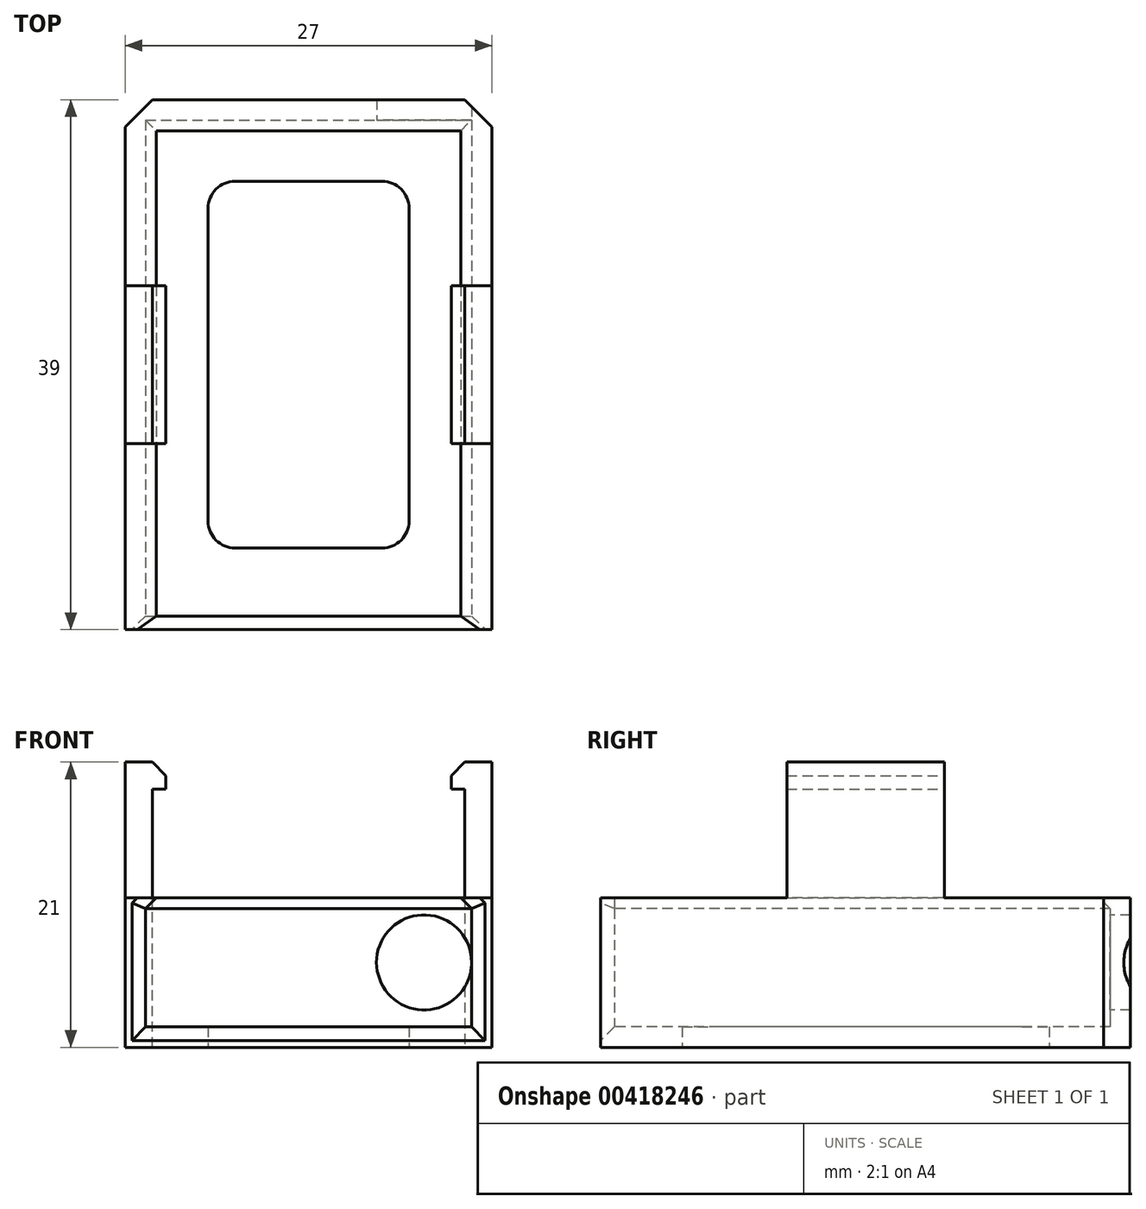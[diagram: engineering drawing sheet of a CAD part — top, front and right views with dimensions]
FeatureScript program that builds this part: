
annotation { "Feature Type Name" : "Feature", "Feature Type Description" : "" }
export const myFeature = defineFeature(function(context is Context, id is Id, definition is map)
    precondition{}
    {
        {
            var Q0;
            Q0=qCreatedBy(makeId("Top.planeOp"),FACE);
            var sketch = newSketch(context, id + "F0", { "sketchPlane" : qUnion([Q0])});
            skPoint(sketch, "E0", {"position": v(0, 0) * mm});
            skLineSegment(sketch, "E1", {"start": v(-12, 19.5) * mm, "end": v(-12, -19.5) * mm});
            skLineSegment(sketch, "E2.MirrorCS", {"start": v(12, 19.5) * mm, "end": v(12, -19.5) * mm});
            skLineSegment(sketch, "E3", {"start": v(-13.5, 19.5) * mm, "end": v(-13.5, -19.5) * mm});
            skLineSegment(sketch, "E4.MirrorCS", {"start": v(13.5, 19.5) * mm, "end": v(13.5, -19.5) * mm});
            skLineSegment(sketch, "E5", {"start": v(-13.5, 19.5) * mm, "end": v(13.5, 19.5) * mm});
            skLineSegment(sketch, "E6.MirrorCS", {"start": v(-13.5, -19.5) * mm, "end": v(13.5, -19.5) * mm});
            skLineSegment(sketch, "E7", {"start": v(-12, 18) * mm, "end": v(12, 18) * mm});
            skLineSegment(sketch, "E8.bottom", {"start": v(7.4, 13.5) * mm, "end": v(-7.4, 13.5) * mm});
            skLineSegment(sketch, "E8.top", {"start": v(7.4, -13.5) * mm, "end": v(-7.4, -13.5) * mm});
            skLineSegment(sketch, "E8.left", {"start": v(7.4, 13.5) * mm, "end": v(7.4, -13.5) * mm});
            skLineSegment(sketch, "E8.right", {"start": v(-7.4, 13.5) * mm, "end": v(-7.4, -13.5) * mm});
            skLineSegment(sketch, "E9", {"start": v(-11.5, 0) * mm, "end": v(-11.5, 5.8) * mm});
            skLineSegment(sketch, "E10.MirrorCS", {"start": v(-11.5, 0) * mm, "end": v(-11.5, -5.8) * mm});
            skLineSegment(sketch, "E11.MirrorCS", {"start": v(11.5, 0) * mm, "end": v(11.5, 5.8) * mm});
            skLineSegment(sketch, "E12.MirrorCS", {"start": v(11.5, 0) * mm, "end": v(11.5, -5.8) * mm});
            skLineSegment(sketch, "E13", {"start": v(-11.5, 5.8) * mm, "end": v(-13.5, 5.8) * mm});
            skLineSegment(sketch, "E14", {"start": v(-11.5, -5.8) * mm, "end": v(-13.5, -5.8) * mm});
            skLineSegment(sketch, "E15", {"start": v(11.5, 5.8) * mm, "end": v(13.5, 5.8) * mm});
            skLineSegment(sketch, "E16", {"start": v(11.5, -5.8) * mm, "end": v(13.5, -5.8) * mm});
            skSolve(sketch);
        }
        {
            var Q0;
            {var subQ0=sQuery(id+"F0.wireOp",EDGE,"E7");Q0=makeQuery(id+"F0.imprint","IMPRINT",FACE,{"disambiguationData":[TD([[makeQuery(id+"F0.imprint","IMPRINT",EDGE,{"derivedFrom":subQ0}),-1.0]])]});}
            extrude(context, id + "F1", {"entities" : qUnion([Q0]), "depth" : 1.5 * mm});
        }
        {
            var Q0;
            {var subQ1=sQuery(id+"F0.wireOp",EDGE,"E9");Q0=makeQuery(id+"F0.imprint","IMPRINT",FACE,{"disambiguationData":[TD([[makeQuery(id+"F0.imprint","IMPRINT",EDGE,{"derivedFrom":subQ1}),1.0]])]});}
            var Q1;
            {var subQ0=sQuery(id+"F0.wireOp",EDGE,"E13");var subQ1=sQuery(id+"F0.wireOp",EDGE,"E1");var subQ2=makeQuery(id+"F0.imprint","INTERSECT",VERTEX,{"derivedFrom":[subQ1,subQ0]});Q1=makeQuery(id+"F0.imprint","IMPRINT",FACE,{"disambiguationData":[TD([[makeQuery(id+"F0.imprint","IMPRINT",EDGE,{"disambiguationData":[TD([[subQ2,-1.0]])],"derivedFrom":subQ1}),-1.0]])]});}
            var Q2;
            {var subQ1=sQuery(id+"F0.wireOp",EDGE,"E11.MirrorCS");Q2=makeQuery(id+"F0.imprint","IMPRINT",FACE,{"disambiguationData":[TD([[makeQuery(id+"F0.imprint","IMPRINT",EDGE,{"derivedFrom":subQ1}),-1.0]])]});}
            var Q3;
            {var subQ0=sQuery(id+"F0.wireOp",EDGE,"E15");var subQ1=sQuery(id+"F0.wireOp",EDGE,"E2.MirrorCS");var subQ2=makeQuery(id+"F0.imprint","INTERSECT",VERTEX,{"derivedFrom":[subQ1,subQ0]});Q3=makeQuery(id+"F0.imprint","IMPRINT",FACE,{"disambiguationData":[TD([[makeQuery(id+"F0.imprint","IMPRINT",EDGE,{"disambiguationData":[TD([[subQ2,-1.0]])],"derivedFrom":subQ1}),1.0]])]});}
            extrude(context, id + "F2", {"entities" : qUnion([Q0, Q1, Q2, Q3]), "operationType" : NewBodyOperationType.ADD, "depth" : 21 * mm});
        }
        {
            var Q0;
            {var subQ3=sQuery(id+"F0.wireOp",EDGE,"E7");Q0=makeQuery(id+"F0.imprint","IMPRINT",FACE,{"disambiguationData":[TD([[makeQuery(id+"F0.imprint","IMPRINT",EDGE,{"derivedFrom":subQ3}),1.0]])]});}
            var Q1;
            {var subQ0=sQuery(id+"F0.wireOp",EDGE,"E5");var subQ1=sQuery(id+"F0.wireOp",EDGE,"E1");var subQ2=makeQuery(id+"F0.imprint","INTERSECT",VERTEX,{"derivedFrom":[subQ1,subQ0]});Q1=makeQuery(id+"F0.imprint","IMPRINT",FACE,{"disambiguationData":[TD([[makeQuery(id+"F0.imprint","IMPRINT",EDGE,{"disambiguationData":[TD([[subQ2,-1.0]])],"derivedFrom":subQ1}),-1.0]])]});}
            var Q2;
            {var subQ0=sQuery(id+"F0.wireOp",EDGE,"E6.MirrorCS");var subQ1=sQuery(id+"F0.wireOp",EDGE,"E1");var subQ2=makeQuery(id+"F0.imprint","INTERSECT",VERTEX,{"derivedFrom":[subQ1,subQ0]});Q2=makeQuery(id+"F0.imprint","IMPRINT",FACE,{"disambiguationData":[TD([[makeQuery(id+"F0.imprint","IMPRINT",EDGE,{"disambiguationData":[TD([[subQ2,1.0]])],"derivedFrom":subQ1}),-1.0]])]});}
            var Q3;
            {var subQ0=sQuery(id+"F0.wireOp",EDGE,"E6.MirrorCS");var subQ1=sQuery(id+"F0.wireOp",EDGE,"E2.MirrorCS");var subQ2=makeQuery(id+"F0.imprint","INTERSECT",VERTEX,{"derivedFrom":[subQ1,subQ0]});Q3=makeQuery(id+"F0.imprint","IMPRINT",FACE,{"disambiguationData":[TD([[makeQuery(id+"F0.imprint","IMPRINT",EDGE,{"disambiguationData":[TD([[subQ2,1.0]])],"derivedFrom":subQ1}),1.0]])]});}
            var Q4;
            {var subQ0=sQuery(id+"F0.wireOp",EDGE,"E5");var subQ1=sQuery(id+"F0.wireOp",EDGE,"E2.MirrorCS");var subQ2=makeQuery(id+"F0.imprint","INTERSECT",VERTEX,{"derivedFrom":[subQ1,subQ0]});Q4=makeQuery(id+"F0.imprint","IMPRINT",FACE,{"disambiguationData":[TD([[makeQuery(id+"F0.imprint","IMPRINT",EDGE,{"disambiguationData":[TD([[subQ2,-1.0]])],"derivedFrom":subQ1}),1.0]])]});}
            extrude(context, id + "F3", {"entities" : qUnion([Q0, Q1, Q2, Q3, Q4]), "operationType" : NewBodyOperationType.ADD, "depth" : 11 * mm});
        }
        {
            var Q0;
            {var subQ1=sQuery(id+"F0.wireOp",EDGE,"E9");Q0=makeQuery(id+"F0.imprint","IMPRINT",FACE,{"disambiguationData":[TD([[makeQuery(id+"F0.imprint","IMPRINT",EDGE,{"derivedFrom":subQ1}),1.0]])]});}
            var Q1;
            {var subQ1=sQuery(id+"F0.wireOp",EDGE,"E11.MirrorCS");Q1=makeQuery(id+"F0.imprint","IMPRINT",FACE,{"disambiguationData":[TD([[makeQuery(id+"F0.imprint","IMPRINT",EDGE,{"derivedFrom":subQ1}),-1.0]])]});}
            extrude(context, id + "F4", {"entities" : qUnion([Q0, Q1]), "operationType" : NewBodyOperationType.REMOVE, "depth" : 11 * mm, "hasSecondDirection" : true, "secondDirectionOppositeDirection" : false, "secondDirectionDepth" : 1.5 * mm});
        }
        {
            var Q0;
            {var subQ0=sQuery(id+"F0.wireOp",EDGE,"E1");Q0=makeQuery(id+"F4.boolean.opBoolean","MERGE",FACE,{"derivedFrom":[makeQuery(id+"F3.opExtrude","SWEPT_FACE",FACE,{"disambiguationData":[OSD([subQ0]),TDD([makeQuery(id+"F0.imprint","IMPRINT",EDGE,{"disambiguationData":[TD([[makeQuery(id+"F0.imprint","INTERSECT",VERTEX,{"derivedFrom":[subQ0,sQuery(id+"F0.wireOp",EDGE,"E7")]}),-1.0]])],"derivedFrom":subQ0})])]}),makeQuery(id+"F3.opExtrude","SWEPT_FACE",FACE,{"disambiguationData":[OSD([subQ0]),TDD([makeQuery(id+"F0.imprint","IMPRINT",EDGE,{"disambiguationData":[TD([[makeQuery(id+"F0.imprint","INTERSECT",VERTEX,{"derivedFrom":[subQ0,sQuery(id+"F0.wireOp",EDGE,"E6.MirrorCS")]}),1.0]])],"derivedFrom":subQ0})])]}),makeQuery(id+"F4.opExtrude","SWEPT_FACE",FACE,{"disambiguationData":[OSD([subQ0])]})]});}
            var sketch = newSketch(context, id + "F5", { "sketchPlane" : qUnion([Q0])});
            skLineSegment(sketch, "E17", {"start": v(18, 10.2) * mm, "end": v(-19.5, 10.2) * mm});
            skSolve(sketch);
        }
        {
            var Q0;
            Q0=makeQuery(id+"F3.opExtrude","SWEPT_FACE",FACE,{"disambiguationData":[OSD([sQuery(id+"F0.wireOp",EDGE,"E7")])]});
            var sketch = newSketch(context, id + "F6", { "sketchPlane" : qUnion([Q0])});
            skLineSegment(sketch, "E18", {"start": v(-12, 10.2) * mm, "end": v(12, 10.2) * mm});
            skSolve(sketch);
        }
        {
            var Q0;
            {var subQ0=sQuery(id+"F0.wireOp",EDGE,"E2.MirrorCS");Q0=makeQuery(id+"F4.boolean.opBoolean","MERGE",FACE,{"derivedFrom":[makeQuery(id+"F3.opExtrude","SWEPT_FACE",FACE,{"disambiguationData":[OSD([subQ0]),TDD([makeQuery(id+"F0.imprint","IMPRINT",EDGE,{"disambiguationData":[TD([[makeQuery(id+"F0.imprint","INTERSECT",VERTEX,{"derivedFrom":[subQ0,sQuery(id+"F0.wireOp",EDGE,"E7")]}),-1.0]])],"derivedFrom":subQ0})])]}),makeQuery(id+"F3.opExtrude","SWEPT_FACE",FACE,{"disambiguationData":[OSD([subQ0]),TDD([makeQuery(id+"F0.imprint","IMPRINT",EDGE,{"disambiguationData":[TD([[makeQuery(id+"F0.imprint","INTERSECT",VERTEX,{"derivedFrom":[subQ0,sQuery(id+"F0.wireOp",EDGE,"E6.MirrorCS")]}),1.0]])],"derivedFrom":subQ0})])]}),makeQuery(id+"F4.opExtrude","SWEPT_FACE",FACE,{"disambiguationData":[OSD([subQ0])]})]});}
            var sketch = newSketch(context, id + "F7", { "sketchPlane" : qUnion([Q0])});
            skLineSegment(sketch, "E19", {"start": v(-18, 10.2) * mm, "end": v(19.5, 10.2) * mm});
            skSolve(sketch);
        }
        {
            var Q0;
            {var subQ5=sQuery(id+"F7.wireOp",EDGE,"E19");Q0=makeQuery(id+"F7.imprint","IMPRINT",FACE,{"disambiguationData":[TD([[makeQuery(id+"F7.imprint","IMPRINT",EDGE,{"derivedFrom":subQ5}),1.0]])]});}
            var Q1;
            Q1=makeQuery(id+"F2.opExtrude","SWEPT_FACE",FACE,{"disambiguationData":[OSD([sQuery(id+"F0.wireOp",EDGE,"E11.MirrorCS"),sQuery(id+"F0.wireOp",EDGE,"E12.MirrorCS")])]});
            extrude(context, id + "F8", {"entities" : qUnion([Q0]), "operationType" : NewBodyOperationType.ADD, "endBoundEntityFace" : qUnion([Q1]), "depth" : 0.8 * mm});
        }
        {
            var Q0;
            {var subQ5=sQuery(id+"F5.wireOp",EDGE,"E17");Q0=makeQuery(id+"F5.imprint","IMPRINT",FACE,{"disambiguationData":[TD([[makeQuery(id+"F5.imprint","IMPRINT",EDGE,{"derivedFrom":subQ5}),-1.0]])]});}
            extrude(context, id + "F9", {"entities" : qUnion([Q0]), "operationType" : NewBodyOperationType.ADD, "depth" : 0.8 * mm});
        }
        {
            var Q0;
            {var subQ0=sQuery(id+"F6.wireOp",EDGE,"E18");Q0=makeQuery(id+"F6.imprint","IMPRINT",FACE,{"disambiguationData":[TD([[makeQuery(id+"F6.imprint","IMPRINT",EDGE,{"derivedFrom":subQ0}),1.0]])]});}
            extrude(context, id + "F10", {"entities" : qUnion([Q0]), "operationType" : NewBodyOperationType.ADD, "depth" : 0.8 * mm});
        }
        {
            var Q0;
            Q0=makeQuery(id+"F9.opExtrude","CAP_EDGE",EDGE,{"disambiguationData":[OSD([sQuery(id+"F5.wireOp",EDGE,"E17")])],"isStart":false});
            var Q1;
            Q1=makeQuery(id+"F10.opExtrude","CAP_EDGE",EDGE,{"disambiguationData":[OSD([sQuery(id+"F6.wireOp",EDGE,"E18")])],"isStart":false});
            var Q2;
            Q2=makeQuery(id+"F8.opExtrude","CAP_EDGE",EDGE,{"disambiguationData":[OSD([sQuery(id+"F7.wireOp",EDGE,"E19")])],"isStart":false});
            var Q3;
            {var subQ0=sQuery(id+"F0.wireOp",EDGE,"E2.MirrorCS");Q3=makeQuery(id+"F4.boolean.opBoolean","MERGE",EDGE,{"derivedFrom":[makeQuery(id+"F1.opExtrude","CAP_EDGE",EDGE,{"disambiguationData":[OSD([subQ0]),TDD([makeQuery(id+"F0.imprint","IMPRINT",EDGE,{"disambiguationData":[TD([[makeQuery(id+"F0.imprint","INTERSECT",VERTEX,{"derivedFrom":[subQ0,sQuery(id+"F0.wireOp",EDGE,"E7")]}),-1.0]])],"derivedFrom":subQ0})])],"isStart":false}),makeQuery(id+"F1.opExtrude","CAP_EDGE",EDGE,{"disambiguationData":[OSD([subQ0]),TDD([makeQuery(id+"F0.imprint","IMPRINT",EDGE,{"disambiguationData":[TD([[makeQuery(id+"F0.imprint","INTERSECT",VERTEX,{"derivedFrom":[subQ0,sQuery(id+"F0.wireOp",EDGE,"E6.MirrorCS")]}),1.0]])],"derivedFrom":subQ0})])],"isStart":false}),makeQuery(id+"F4.opExtrude","CAP_EDGE",EDGE,{"disambiguationData":[OSD([subQ0])],"isStart":true})]});}
            var Q4;
            {var subQ0=sQuery(id+"F0.wireOp",EDGE,"E1");Q4=makeQuery(id+"F4.boolean.opBoolean","MERGE",EDGE,{"derivedFrom":[makeQuery(id+"F1.opExtrude","CAP_EDGE",EDGE,{"disambiguationData":[OSD([subQ0]),TDD([makeQuery(id+"F0.imprint","IMPRINT",EDGE,{"disambiguationData":[TD([[makeQuery(id+"F0.imprint","INTERSECT",VERTEX,{"derivedFrom":[subQ0,sQuery(id+"F0.wireOp",EDGE,"E7")]}),-1.0]])],"derivedFrom":subQ0})])],"isStart":false}),makeQuery(id+"F1.opExtrude","CAP_EDGE",EDGE,{"disambiguationData":[OSD([subQ0]),TDD([makeQuery(id+"F0.imprint","IMPRINT",EDGE,{"disambiguationData":[TD([[makeQuery(id+"F0.imprint","INTERSECT",VERTEX,{"derivedFrom":[subQ0,sQuery(id+"F0.wireOp",EDGE,"E6.MirrorCS")]}),1.0]])],"derivedFrom":subQ0})])],"isStart":false}),makeQuery(id+"F4.opExtrude","CAP_EDGE",EDGE,{"disambiguationData":[OSD([subQ0])],"isStart":true})]});}
            var Q5;
            Q5=makeQuery(id+"F1.opExtrude","CAP_EDGE",EDGE,{"disambiguationData":[OSD([sQuery(id+"F0.wireOp",EDGE,"E7")])],"isStart":false});
            chamfer(context, id + "F11", {"entities" : qUnion([Q0, Q1, Q2, Q3, Q4, Q5]), "width" : 0.8 * mm, "tangentPropagation" : true});
        }
        {
            var Q0;
            Q0=makeQuery(id+"F3.opExtrude","SWEPT_EDGE",EDGE,{"disambiguationData":[OSD([sQuery(id+"F0.wireOp",EDGE,"E4.MirrorCS"),sQuery(id+"F0.wireOp",EDGE,"E5")])]});
            var Q1;
            Q1=makeQuery(id+"F3.opExtrude","SWEPT_EDGE",EDGE,{"disambiguationData":[OSD([sQuery(id+"F0.wireOp",EDGE,"E3"),sQuery(id+"F0.wireOp",EDGE,"E5")])]});
            chamfer(context, id + "F12", {"entities" : qUnion([Q0, Q1]), "width" : 2 * mm, "tangentPropagation" : true});
        }
        {
            var Q0;
            Q0=makeQuery(id+"F2.opExtrude","SWEPT_FACE",FACE,{"disambiguationData":[OSD([sQuery(id+"F0.wireOp",EDGE,"E9"),sQuery(id+"F0.wireOp",EDGE,"E10.MirrorCS")])]});
            var sketch = newSketch(context, id + "F13", { "sketchPlane" : qUnion([Q0])});
            skLineSegment(sketch, "E20", {"start": v(-5.8, 19) * mm, "end": v(5.8, 19) * mm});
            skSolve(sketch);
        }
        {
            var Q0;
            Q0=makeQuery(id+"F2.opExtrude","SWEPT_FACE",FACE,{"disambiguationData":[OSD([sQuery(id+"F0.wireOp",EDGE,"E11.MirrorCS"),sQuery(id+"F0.wireOp",EDGE,"E12.MirrorCS")])]});
            var sketch = newSketch(context, id + "F14", { "sketchPlane" : qUnion([Q0])});
            skLineSegment(sketch, "E21", {"start": v(5.8, 19) * mm, "end": v(-5.8, 19) * mm});
            skSolve(sketch);
        }
        {
            var Q0;
            {var subQ0=sQuery(id+"F14.wireOp",EDGE,"E21");Q0=makeQuery(id+"F14.imprint","IMPRINT",FACE,{"disambiguationData":[TD([[makeQuery(id+"F14.imprint","IMPRINT",EDGE,{"derivedFrom":subQ0}),-1.0]])]});}
            extrude(context, id + "F15", {"entities" : qUnion([Q0]), "operationType" : NewBodyOperationType.ADD, "depth" : 1 * mm});
        }
        {
            var Q0;
            {var subQ0=sQuery(id+"F13.wireOp",EDGE,"E20");Q0=makeQuery(id+"F13.imprint","IMPRINT",FACE,{"disambiguationData":[TD([[makeQuery(id+"F13.imprint","IMPRINT",EDGE,{"derivedFrom":subQ0}),1.0]])]});}
            extrude(context, id + "F16", {"entities" : qUnion([Q0]), "operationType" : NewBodyOperationType.ADD, "depth" : 1 * mm});
        }
        {
            var Q0;
            Q0=makeQuery(id+"F16.opExtrude","CAP_EDGE",EDGE,{"disambiguationData":[OSD([sQuery(id+"F0.wireOp",EDGE,"E9"),sQuery(id+"F0.wireOp",EDGE,"E10.MirrorCS")])],"isStart":false});
            var Q1;
            Q1=makeQuery(id+"F15.opExtrude","CAP_EDGE",EDGE,{"disambiguationData":[OSD([sQuery(id+"F0.wireOp",EDGE,"E11.MirrorCS"),sQuery(id+"F0.wireOp",EDGE,"E12.MirrorCS")])],"isStart":false});
            chamfer(context, id + "F17", {"entities" : qUnion([Q0, Q1]), "width" : 1 * mm, "tangentPropagation" : true});
        }
        {
            var Q0;
            Q0=makeQuery(id+"F1.opExtrude","CAP_EDGE",EDGE,{"disambiguationData":[OSD([sQuery(id+"F0.wireOp",EDGE,"E6.MirrorCS")])],"isStart":false});
            var Q1;
            Q1=makeQuery(id+"F3.opExtrude","SWEPT_EDGE",EDGE,{"disambiguationData":[OSD([sQuery(id+"F0.wireOp",EDGE,"E2.MirrorCS"),sQuery(id+"F0.wireOp",EDGE,"E6.MirrorCS")])]});
            var Q2;
            {var subQ0=sQuery(id+"F0.wireOp",EDGE,"E6.MirrorCS");var subQ1=sQuery(id+"F0.wireOp",EDGE,"E1");var subQ2=sQuery(id+"F0.wireOp",EDGE,"E2.MirrorCS");var subQ3=makeQuery(id+"F0.imprint","INTERSECT",VERTEX,{"derivedFrom":[subQ2,subQ0]});Q2=makeQuery(id+"F11.opChamfer","BLEND_EDGE",EDGE,{"blendedFrom":[makeQuery(id+"F4.boolean.opBoolean","MERGE",EDGE,{"derivedFrom":[makeQuery(id+"F1.opExtrude","CAP_EDGE",EDGE,{"disambiguationData":[OSD([subQ2]),TDD([makeQuery(id+"F0.imprint","IMPRINT",EDGE,{"disambiguationData":[TD([[makeQuery(id+"F0.imprint","INTERSECT",VERTEX,{"derivedFrom":[subQ2,sQuery(id+"F0.wireOp",EDGE,"E7")]}),-1.0]])],"derivedFrom":subQ2})])],"isStart":false}),makeQuery(id+"F1.opExtrude","CAP_EDGE",EDGE,{"disambiguationData":[OSD([subQ2]),TDD([makeQuery(id+"F0.imprint","IMPRINT",EDGE,{"disambiguationData":[TD([[subQ3,1.0]])],"derivedFrom":subQ2})])],"isStart":false}),makeQuery(id+"F4.opExtrude","CAP_EDGE",EDGE,{"disambiguationData":[OSD([subQ2])],"isStart":true})]}),makeQuery(id+"F9.boolean.opBoolean","MERGE",FACE,{"derivedFrom":[makeQuery(id+"F8.boolean.opBoolean","MERGE",FACE,{"derivedFrom":[makeQuery(id+"F3.boolean.opBoolean","MERGE",FACE,{"derivedFrom":[makeQuery(id+"F1.opExtrude","SWEPT_FACE",FACE,{"disambiguationData":[OSD([subQ0])]}),makeQuery(id+"F3.opExtrude","SWEPT_FACE",FACE,{"disambiguationData":[OSD([subQ0]),TDD([makeQuery(id+"F0.imprint","IMPRINT",EDGE,{"disambiguationData":[TD([[makeQuery(id+"F0.imprint","INTERSECT",VERTEX,{"derivedFrom":[subQ1,subQ0]}),1.0]])],"derivedFrom":subQ0})])]}),makeQuery(id+"F3.opExtrude","SWEPT_FACE",FACE,{"disambiguationData":[OSD([subQ0]),TDD([makeQuery(id+"F0.imprint","IMPRINT",EDGE,{"disambiguationData":[TD([[subQ3,-1.0]])],"derivedFrom":subQ0})])]})]}),makeQuery(id+"F8.opExtrude","SWEPT_FACE",FACE,{"disambiguationData":[OSD([subQ2,subQ0])]})]}),makeQuery(id+"F9.opExtrude","SWEPT_FACE",FACE,{"disambiguationData":[OSD([subQ1,subQ0])]})]})],"blendedInto":[makeQuery(id+"F9.boolean.opBoolean","MERGE",FACE,{"derivedFrom":[makeQuery(id+"F8.boolean.opBoolean","MERGE",FACE,{"derivedFrom":[makeQuery(id+"F3.boolean.opBoolean","MERGE",FACE,{"derivedFrom":[makeQuery(id+"F1.opExtrude","SWEPT_FACE",FACE,{"disambiguationData":[OSD([subQ0])]}),makeQuery(id+"F3.opExtrude","SWEPT_FACE",FACE,{"disambiguationData":[OSD([subQ0]),TDD([makeQuery(id+"F0.imprint","IMPRINT",EDGE,{"disambiguationData":[TD([[makeQuery(id+"F0.imprint","INTERSECT",VERTEX,{"derivedFrom":[subQ1,subQ0]}),1.0]])],"derivedFrom":subQ0})])]}),makeQuery(id+"F3.opExtrude","SWEPT_FACE",FACE,{"disambiguationData":[OSD([subQ0]),TDD([makeQuery(id+"F0.imprint","IMPRINT",EDGE,{"disambiguationData":[TD([[subQ3,-1.0]])],"derivedFrom":subQ0})])]})]}),makeQuery(id+"F8.opExtrude","SWEPT_FACE",FACE,{"disambiguationData":[OSD([subQ2,subQ0])]})]}),makeQuery(id+"F9.opExtrude","SWEPT_FACE",FACE,{"disambiguationData":[OSD([subQ1,subQ0])]})]})]});}
            var Q3;
            Q3=makeQuery(id+"F3.opExtrude","SWEPT_EDGE",EDGE,{"disambiguationData":[OSD([sQuery(id+"F0.wireOp",EDGE,"E1"),sQuery(id+"F0.wireOp",EDGE,"E6.MirrorCS")])]});
            var Q4;
            {var subQ0=sQuery(id+"F0.wireOp",EDGE,"E6.MirrorCS");var subQ1=sQuery(id+"F0.wireOp",EDGE,"E1");var subQ2=sQuery(id+"F0.wireOp",EDGE,"E2.MirrorCS");var subQ3=makeQuery(id+"F0.imprint","INTERSECT",VERTEX,{"derivedFrom":[subQ1,subQ0]});Q4=makeQuery(id+"F11.opChamfer","BLEND_EDGE",EDGE,{"blendedFrom":[makeQuery(id+"F4.boolean.opBoolean","MERGE",EDGE,{"derivedFrom":[makeQuery(id+"F1.opExtrude","CAP_EDGE",EDGE,{"disambiguationData":[OSD([subQ1]),TDD([makeQuery(id+"F0.imprint","IMPRINT",EDGE,{"disambiguationData":[TD([[makeQuery(id+"F0.imprint","INTERSECT",VERTEX,{"derivedFrom":[subQ1,sQuery(id+"F0.wireOp",EDGE,"E7")]}),-1.0]])],"derivedFrom":subQ1})])],"isStart":false}),makeQuery(id+"F1.opExtrude","CAP_EDGE",EDGE,{"disambiguationData":[OSD([subQ1]),TDD([makeQuery(id+"F0.imprint","IMPRINT",EDGE,{"disambiguationData":[TD([[subQ3,1.0]])],"derivedFrom":subQ1})])],"isStart":false}),makeQuery(id+"F4.opExtrude","CAP_EDGE",EDGE,{"disambiguationData":[OSD([subQ1])],"isStart":true})]}),makeQuery(id+"F9.boolean.opBoolean","MERGE",FACE,{"derivedFrom":[makeQuery(id+"F8.boolean.opBoolean","MERGE",FACE,{"derivedFrom":[makeQuery(id+"F3.boolean.opBoolean","MERGE",FACE,{"derivedFrom":[makeQuery(id+"F1.opExtrude","SWEPT_FACE",FACE,{"disambiguationData":[OSD([subQ0])]}),makeQuery(id+"F3.opExtrude","SWEPT_FACE",FACE,{"disambiguationData":[OSD([subQ0]),TDD([makeQuery(id+"F0.imprint","IMPRINT",EDGE,{"disambiguationData":[TD([[subQ3,1.0]])],"derivedFrom":subQ0})])]}),makeQuery(id+"F3.opExtrude","SWEPT_FACE",FACE,{"disambiguationData":[OSD([subQ0]),TDD([makeQuery(id+"F0.imprint","IMPRINT",EDGE,{"disambiguationData":[TD([[makeQuery(id+"F0.imprint","INTERSECT",VERTEX,{"derivedFrom":[subQ2,subQ0]}),-1.0]])],"derivedFrom":subQ0})])]})]}),makeQuery(id+"F8.opExtrude","SWEPT_FACE",FACE,{"disambiguationData":[OSD([subQ2,subQ0])]})]}),makeQuery(id+"F9.opExtrude","SWEPT_FACE",FACE,{"disambiguationData":[OSD([subQ1,subQ0])]})]})],"blendedInto":[makeQuery(id+"F9.boolean.opBoolean","MERGE",FACE,{"derivedFrom":[makeQuery(id+"F8.boolean.opBoolean","MERGE",FACE,{"derivedFrom":[makeQuery(id+"F3.boolean.opBoolean","MERGE",FACE,{"derivedFrom":[makeQuery(id+"F1.opExtrude","SWEPT_FACE",FACE,{"disambiguationData":[OSD([subQ0])]}),makeQuery(id+"F3.opExtrude","SWEPT_FACE",FACE,{"disambiguationData":[OSD([subQ0]),TDD([makeQuery(id+"F0.imprint","IMPRINT",EDGE,{"disambiguationData":[TD([[subQ3,1.0]])],"derivedFrom":subQ0})])]}),makeQuery(id+"F3.opExtrude","SWEPT_FACE",FACE,{"disambiguationData":[OSD([subQ0]),TDD([makeQuery(id+"F0.imprint","IMPRINT",EDGE,{"disambiguationData":[TD([[makeQuery(id+"F0.imprint","INTERSECT",VERTEX,{"derivedFrom":[subQ2,subQ0]}),-1.0]])],"derivedFrom":subQ0})])]})]}),makeQuery(id+"F8.opExtrude","SWEPT_FACE",FACE,{"disambiguationData":[OSD([subQ2,subQ0])]})]}),makeQuery(id+"F9.opExtrude","SWEPT_FACE",FACE,{"disambiguationData":[OSD([subQ1,subQ0])]})]})]});}
            var Q5;
            {var subQ0=sQuery(id+"F0.wireOp",EDGE,"E6.MirrorCS");var subQ1=sQuery(id+"F0.wireOp",EDGE,"E1");var subQ2=sQuery(id+"F0.wireOp",EDGE,"E2.MirrorCS");Q5=makeQuery(id+"F11.opChamfer","BLEND_EDGE",EDGE,{"blendedFrom":[makeQuery(id+"F9.opExtrude","CAP_EDGE",EDGE,{"disambiguationData":[OSD([sQuery(id+"F5.wireOp",EDGE,"E17")])],"isStart":false}),makeQuery(id+"F9.boolean.opBoolean","MERGE",FACE,{"derivedFrom":[makeQuery(id+"F8.boolean.opBoolean","MERGE",FACE,{"derivedFrom":[makeQuery(id+"F3.boolean.opBoolean","MERGE",FACE,{"derivedFrom":[makeQuery(id+"F1.opExtrude","SWEPT_FACE",FACE,{"disambiguationData":[OSD([subQ0])]}),makeQuery(id+"F3.opExtrude","SWEPT_FACE",FACE,{"disambiguationData":[OSD([subQ0]),TDD([makeQuery(id+"F0.imprint","IMPRINT",EDGE,{"disambiguationData":[TD([[makeQuery(id+"F0.imprint","INTERSECT",VERTEX,{"derivedFrom":[subQ1,subQ0]}),1.0]])],"derivedFrom":subQ0})])]}),makeQuery(id+"F3.opExtrude","SWEPT_FACE",FACE,{"disambiguationData":[OSD([subQ0]),TDD([makeQuery(id+"F0.imprint","IMPRINT",EDGE,{"disambiguationData":[TD([[makeQuery(id+"F0.imprint","INTERSECT",VERTEX,{"derivedFrom":[subQ2,subQ0]}),-1.0]])],"derivedFrom":subQ0})])]})]}),makeQuery(id+"F8.opExtrude","SWEPT_FACE",FACE,{"disambiguationData":[OSD([subQ2,subQ0])]})]}),makeQuery(id+"F9.opExtrude","SWEPT_FACE",FACE,{"disambiguationData":[OSD([subQ1,subQ0])]})]})],"blendedInto":[makeQuery(id+"F9.boolean.opBoolean","MERGE",FACE,{"derivedFrom":[makeQuery(id+"F8.boolean.opBoolean","MERGE",FACE,{"derivedFrom":[makeQuery(id+"F3.boolean.opBoolean","MERGE",FACE,{"derivedFrom":[makeQuery(id+"F1.opExtrude","SWEPT_FACE",FACE,{"disambiguationData":[OSD([subQ0])]}),makeQuery(id+"F3.opExtrude","SWEPT_FACE",FACE,{"disambiguationData":[OSD([subQ0]),TDD([makeQuery(id+"F0.imprint","IMPRINT",EDGE,{"disambiguationData":[TD([[makeQuery(id+"F0.imprint","INTERSECT",VERTEX,{"derivedFrom":[subQ1,subQ0]}),1.0]])],"derivedFrom":subQ0})])]}),makeQuery(id+"F3.opExtrude","SWEPT_FACE",FACE,{"disambiguationData":[OSD([subQ0]),TDD([makeQuery(id+"F0.imprint","IMPRINT",EDGE,{"disambiguationData":[TD([[makeQuery(id+"F0.imprint","INTERSECT",VERTEX,{"derivedFrom":[subQ2,subQ0]}),-1.0]])],"derivedFrom":subQ0})])]})]}),makeQuery(id+"F8.opExtrude","SWEPT_FACE",FACE,{"disambiguationData":[OSD([subQ2,subQ0])]})]}),makeQuery(id+"F9.opExtrude","SWEPT_FACE",FACE,{"disambiguationData":[OSD([subQ1,subQ0])]})]})]});}
            var Q6;
            {var subQ0=sQuery(id+"F0.wireOp",EDGE,"E6.MirrorCS");var subQ1=sQuery(id+"F0.wireOp",EDGE,"E1");var subQ2=sQuery(id+"F0.wireOp",EDGE,"E2.MirrorCS");Q6=makeQuery(id+"F11.opChamfer","BLEND_EDGE",EDGE,{"blendedFrom":[makeQuery(id+"F8.opExtrude","CAP_EDGE",EDGE,{"disambiguationData":[OSD([sQuery(id+"F7.wireOp",EDGE,"E19")])],"isStart":false}),makeQuery(id+"F9.boolean.opBoolean","MERGE",FACE,{"derivedFrom":[makeQuery(id+"F8.boolean.opBoolean","MERGE",FACE,{"derivedFrom":[makeQuery(id+"F3.boolean.opBoolean","MERGE",FACE,{"derivedFrom":[makeQuery(id+"F1.opExtrude","SWEPT_FACE",FACE,{"disambiguationData":[OSD([subQ0])]}),makeQuery(id+"F3.opExtrude","SWEPT_FACE",FACE,{"disambiguationData":[OSD([subQ0]),TDD([makeQuery(id+"F0.imprint","IMPRINT",EDGE,{"disambiguationData":[TD([[makeQuery(id+"F0.imprint","INTERSECT",VERTEX,{"derivedFrom":[subQ1,subQ0]}),1.0]])],"derivedFrom":subQ0})])]}),makeQuery(id+"F3.opExtrude","SWEPT_FACE",FACE,{"disambiguationData":[OSD([subQ0]),TDD([makeQuery(id+"F0.imprint","IMPRINT",EDGE,{"disambiguationData":[TD([[makeQuery(id+"F0.imprint","INTERSECT",VERTEX,{"derivedFrom":[subQ2,subQ0]}),-1.0]])],"derivedFrom":subQ0})])]})]}),makeQuery(id+"F8.opExtrude","SWEPT_FACE",FACE,{"disambiguationData":[OSD([subQ2,subQ0])]})]}),makeQuery(id+"F9.opExtrude","SWEPT_FACE",FACE,{"disambiguationData":[OSD([subQ1,subQ0])]})]})],"blendedInto":[makeQuery(id+"F9.boolean.opBoolean","MERGE",FACE,{"derivedFrom":[makeQuery(id+"F8.boolean.opBoolean","MERGE",FACE,{"derivedFrom":[makeQuery(id+"F3.boolean.opBoolean","MERGE",FACE,{"derivedFrom":[makeQuery(id+"F1.opExtrude","SWEPT_FACE",FACE,{"disambiguationData":[OSD([subQ0])]}),makeQuery(id+"F3.opExtrude","SWEPT_FACE",FACE,{"disambiguationData":[OSD([subQ0]),TDD([makeQuery(id+"F0.imprint","IMPRINT",EDGE,{"disambiguationData":[TD([[makeQuery(id+"F0.imprint","INTERSECT",VERTEX,{"derivedFrom":[subQ1,subQ0]}),1.0]])],"derivedFrom":subQ0})])]}),makeQuery(id+"F3.opExtrude","SWEPT_FACE",FACE,{"disambiguationData":[OSD([subQ0]),TDD([makeQuery(id+"F0.imprint","IMPRINT",EDGE,{"disambiguationData":[TD([[makeQuery(id+"F0.imprint","INTERSECT",VERTEX,{"derivedFrom":[subQ2,subQ0]}),-1.0]])],"derivedFrom":subQ0})])]})]}),makeQuery(id+"F8.opExtrude","SWEPT_FACE",FACE,{"disambiguationData":[OSD([subQ2,subQ0])]})]}),makeQuery(id+"F9.opExtrude","SWEPT_FACE",FACE,{"disambiguationData":[OSD([subQ1,subQ0])]})]})]});}
            chamfer(context, id + "F18", {"entities" : qUnion([Q0, Q1, Q2, Q3, Q4, Q5, Q6]), "width" : 1 * mm, "tangentPropagation" : true});
        }
        {
            var Q0;
            Q0=makeQuery(id+"F1.opExtrude","SWEPT_EDGE",EDGE,{"disambiguationData":[OSD([sQuery(id+"F0.wireOp",EDGE,"E8.bottom"),sQuery(id+"F0.wireOp",EDGE,"E8.right")])]});
            var Q1;
            Q1=makeQuery(id+"F1.opExtrude","SWEPT_EDGE",EDGE,{"disambiguationData":[OSD([sQuery(id+"F0.wireOp",EDGE,"E8.bottom"),sQuery(id+"F0.wireOp",EDGE,"E8.left")])]});
            var Q2;
            Q2=makeQuery(id+"F1.opExtrude","SWEPT_EDGE",EDGE,{"disambiguationData":[OSD([sQuery(id+"F0.wireOp",EDGE,"E8.top"),sQuery(id+"F0.wireOp",EDGE,"E8.right")])]});
            var Q3;
            Q3=makeQuery(id+"F1.opExtrude","SWEPT_EDGE",EDGE,{"disambiguationData":[OSD([sQuery(id+"F0.wireOp",EDGE,"E8.top"),sQuery(id+"F0.wireOp",EDGE,"E8.left")])]});
            fillet(context, id + "F19", {"entities" : qUnion([Q0, Q1, Q2, Q3]), "radius" : 2 * mm, "tangentPropagation" : true, "allowEdgeOverflow" : false});
        }
        {
            var Q0;
            Q0=makeQuery(id+"F3.opExtrude","SWEPT_FACE",FACE,{"disambiguationData":[OSD([sQuery(id+"F0.wireOp",EDGE,"E7")])]});
            var sketch = newSketch(context, id + "F20", { "sketchPlane" : qUnion([Q0])});
            skCircle(sketch, "E22", {"center": v(8.5, 6.25) * mm, "radius": 3.5 * mm});
            skSolve(sketch);
        }
        {
            var Q0;
            Q0=makeQuery(id+"F20.imprint","IMPRINT",FACE,{"disambiguationData":[TD([[makeQuery(id+"F20.imprint","IMPRINT",EDGE,{"derivedFrom":sQuery(id+"F20.wireOp",EDGE,"E22")}),1.0]])]});
            extrude(context, id + "F21", {"entities" : qUnion([Q0]), "operationType" : NewBodyOperationType.REMOVE, "oppositeDirection" : true, "depth" : 1.5 * mm});
        }
    });
